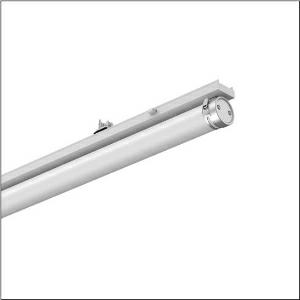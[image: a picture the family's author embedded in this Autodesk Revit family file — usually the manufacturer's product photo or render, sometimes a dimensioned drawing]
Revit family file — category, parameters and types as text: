
# Revit family: monsun_31_tube_51ft10nn4a0atr2
name_source: partatom
category: Lighting Fixtures
units: mm (PartAtom-declared; Revit-internal decimal feet)

## family parameters
Cut with Voids When Loaded = No
Host = Face
Light Source = No
Part Type = Normal
Room Calculation Point = No
Round Connector Dimension = Use Diameter
Shared = No

## types (1)
- --- (1 x LED, 10000 lm, 58 W, 4000K)
    Apparent Load = 58 VA
    CIE Flux Codes = 42 71 90 91 100
    Color Rendering = 80
    Color Temperature = 4000K
    Default Elevation = 1800 mm
    Description = Monsun 31 Tube, tubular luminaire, primary optical cover: diffuser, of PMMA, light emission: direct distribution, primary light characteristic: symmetric, LED, rated luminous flux: 10.000lm, luminous efficacy: 172lm/W, light colour: 840, colour temperature: 4000K, control gear: DALI Multilumen, with with 1 terminal, 5-pole, max. 2.5mm², mains connection: 220..240V, AC, 50/60Hz, rated input power: 58W, housing, cylindrical, of PMMA, semi-transparent, matt white, with luminaire and ceiling fastening, V4A, mounting with brackets of stainless steel, length: 1.500mm, diameter: 75mm, end cap, of stainless steel (V4A), protection rating (complete): IP20, protection rating (lamp compartment): IP67/69K, insulation class (complete): insulation class I (protective earthing), certification: CE, UKCA, impact resistance: IK06, permissible operating ambient temperature: -20..+40°C, corresponds to IFS (International Featured Standards) requirements for safety and quality in the food industry, contact your sales advisor before using the luminaires in applications with unclear chemical exposure, large temperature fluctuations or condensation-forming humidity, packaging unit: 1 piece
    Height = 132 mm
    Lamp = 1 x LED
    Lamp Light Flux = 10000 lm
    Lamp Power = 58 W
    Lamp count = 1
    Length = 1500 mm
    Luminous efficacy = 172 lm/W
    Manufacturer = Siteco
    ModVariant = No
    Model = 51FT10NN4A0ATR2
    Mounting Place = Ceiling
    Mounting Type = Pendant
    Number of Poles = 1
    OnlyDefault = Yes
    Power Factor = 1
    Product Name = Monsun 31 Tube
    Product group = tubular luminaire
    ProductGroupID = 906
    Protection Class = Protection class I
    Protection Degree = IP 20
    RLX_Detail_Level = 1
    RLX_Emergency_Light_Flux = 0 lm
    RLX_Emergency_Type = 0
    RLX_Emergency_Type_DB = No
    RlxData = <blob elided: 32317 chars, md5=3ad59210>
    Socket = socket
    Standby Power = 0 W
    System Light Flux = 10000 lm
    System Power = 58 W
    Type Comments = individual setting: luminous flux: 100 % | (OFF | OFF | ON | OFF) | 350 mA
    Type Image = l_1242814.jpg
    URL = http://relux.com
    VarID = @adj_142849
    Voltage = 0 V
    Weight = 0.00 kg
    Width = 79 mm

## geometry (parser evidence)
native form markers: Blend x4, Sweep x12
no freeform markers — native parametric forms only
